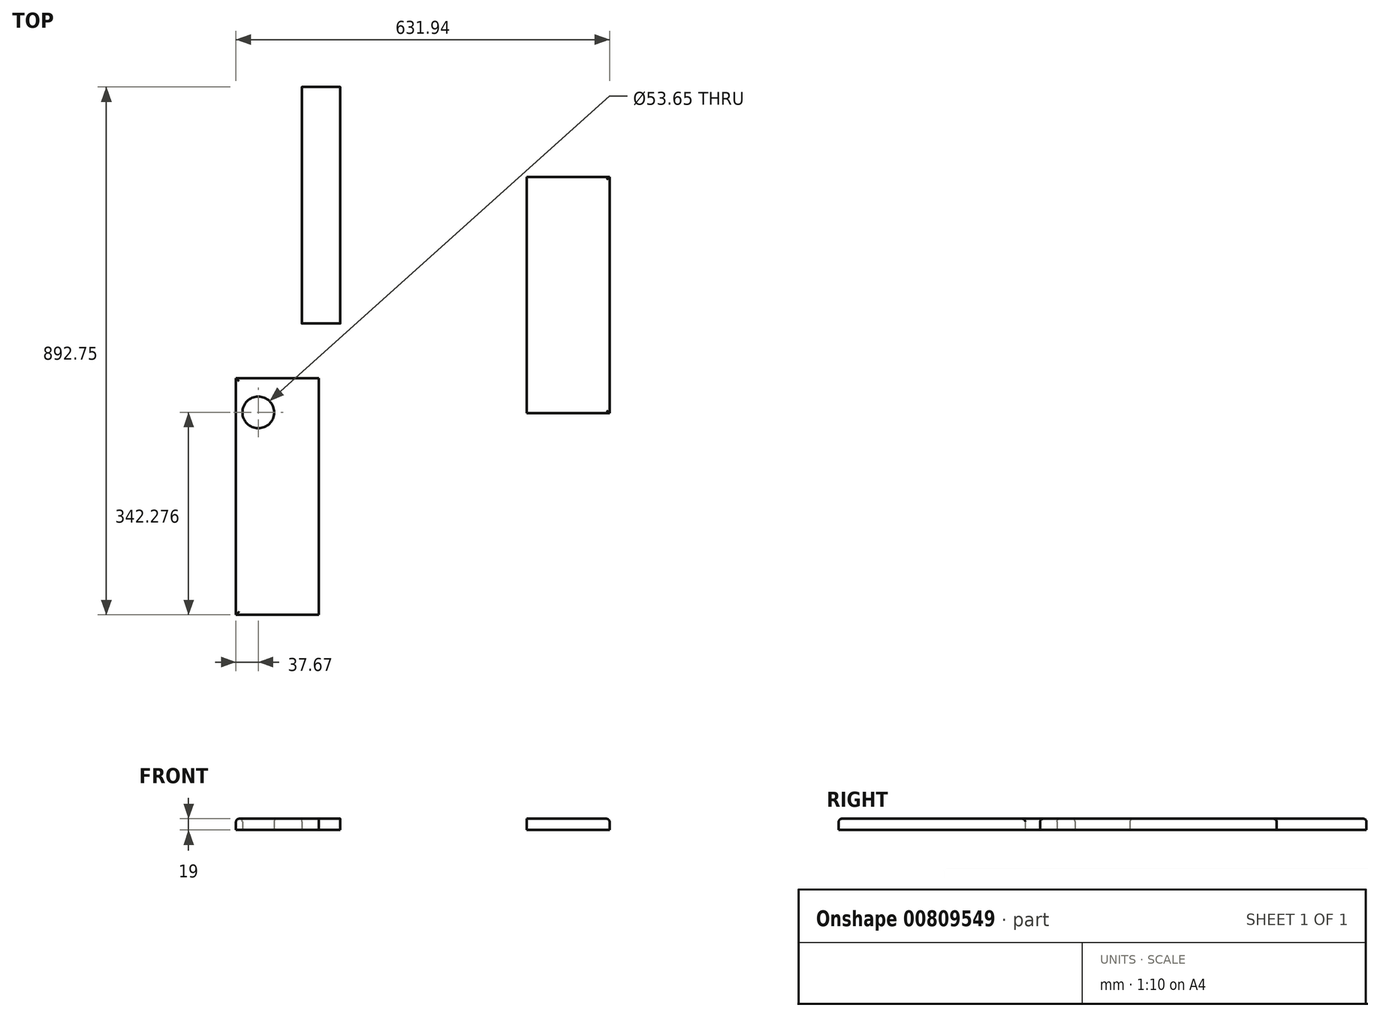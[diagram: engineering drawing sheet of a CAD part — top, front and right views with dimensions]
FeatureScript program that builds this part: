
annotation { "Feature Type Name" : "Feature", "Feature Type Description" : "" }
export const myFeature = defineFeature(function(context is Context, id is Id, definition is map)
    precondition{}
    {
        {
            var Q0;
            Q0=qCreatedBy(makeId("Top.planeOp"),FACE);
            var sketch = newSketch(context, id + "F0", { "sketchPlane" : qUnion([Q0])});
            skLineSegment(sketch, "E0.bottom", {"start": v(-171.23, -176.51) * mm, "end": v(-31.23, -176.51) * mm});
            skLineSegment(sketch, "E0.top", {"start": v(-171.23, 223.49) * mm, "end": v(-31.23, 223.49) * mm});
            skLineSegment(sketch, "E0.left", {"start": v(-171.23, -176.51) * mm, "end": v(-171.23, 223.49) * mm});
            skLineSegment(sketch, "E0.right", {"start": v(-31.23, -176.51) * mm, "end": v(-31.23, 223.49) * mm});
            skSolve(sketch);
        }
        {
            var Q0;
            Q0=makeQuery(id+"F0.imprint","IMPRINT",FACE,{"disambiguationData":[TD([[makeQuery(id+"F0.imprint","IMPRINT",EDGE,{"derivedFrom":sQuery(id+"F0.wireOp",EDGE,"E0.bottom")}),1.0]])]});
            extrude(context, id + "F1", {"entities" : qUnion([Q0]), "depth" : 19 * mm, "offsetDistance" : 25 * mm});
        }
        {
            var Q0;
            Q0=qCreatedBy(makeId("Top.planeOp"),FACE);
            var sketch = newSketch(context, id + "F2", { "sketchPlane" : qUnion([Q0])});
            skLineSegment(sketch, "E1.bottom", {"start": v(-551.77, 375.45) * mm, "end": v(-486.77, 375.45) * mm});
            skLineSegment(sketch, "E1.top", {"start": v(-551.77, -24.55) * mm, "end": v(-486.77, -24.55) * mm});
            skLineSegment(sketch, "E1.left", {"start": v(-551.77, 375.45) * mm, "end": v(-551.77, -24.55) * mm});
            skLineSegment(sketch, "E1.right", {"start": v(-486.77, 375.45) * mm, "end": v(-486.77, -24.55) * mm});
            skSolve(sketch);
        }
        {
            var Q0;
            Q0=makeQuery(id+"F2.imprint","IMPRINT",FACE,{"disambiguationData":[TD([[makeQuery(id+"F2.imprint","IMPRINT",EDGE,{"derivedFrom":sQuery(id+"F2.wireOp",EDGE,"E1.bottom")}),-1.0]])]});
            extrude(context, id + "F3", {"entities" : qUnion([Q0]), "depth" : 19 * mm, "offsetDistance" : 25 * mm});
        }
        {
            var Q0;
            Q0=qCreatedBy(makeId("Top.planeOp"),FACE);
            var sketch = newSketch(context, id + "F4", { "sketchPlane" : qUnion([Q0])});
            skLineSegment(sketch, "E2.bottom", {"start": v(-663.17, -117.3) * mm, "end": v(-523.17, -117.3) * mm});
            skLineSegment(sketch, "E2.top", {"start": v(-663.17, -517.3) * mm, "end": v(-523.17, -517.3) * mm});
            skLineSegment(sketch, "E2.left", {"start": v(-663.17, -117.3) * mm, "end": v(-663.17, -517.3) * mm});
            skLineSegment(sketch, "E2.right", {"start": v(-523.17, -117.3) * mm, "end": v(-523.17, -517.3) * mm});
            skCircle(sketch, "E3", {"center": v(-625.5, -175.02) * mm, "radius": 26.82 * mm});
            skSolve(sketch);
        }
        {
            var Q0;
            Q0 = qSketchRegion(id + "F4", true);
            extrude(context, id + "F5", {"entities" : qUnion([Q0]), "depth" : 19 * mm, "offsetDistance" : 25 * mm});
        }
        {
            var Q0;
            Q0=makeQuery(id+"F5.opExtrude","CAP_EDGE",EDGE,{"disambiguationData":[OSD([sQuery(id+"F4.wireOp",EDGE,"E2.left")])],"isStart":false});
            var Q1;
            Q1=makeQuery(id+"F5.opExtrude","CAP_EDGE",EDGE,{"disambiguationData":[OSD([sQuery(id+"F4.wireOp",EDGE,"E2.top")])],"isStart":false});
            var Q2;
            Q2=makeQuery(id+"F5.opExtrude","CAP_EDGE",EDGE,{"disambiguationData":[OSD([sQuery(id+"F4.wireOp",EDGE,"E2.bottom")])],"isStart":false});
            var Q3;
            Q3=makeQuery(id+"F3.opExtrude","CAP_EDGE",EDGE,{"disambiguationData":[OSD([sQuery(id+"F2.wireOp",EDGE,"E1.top")])],"isStart":false});
            var Q4;
            Q4=makeQuery(id+"F3.opExtrude","CAP_EDGE",EDGE,{"disambiguationData":[OSD([sQuery(id+"F2.wireOp",EDGE,"E1.bottom")])],"isStart":false});
            var Q5;
            Q5=makeQuery(id+"F1.opExtrude","CAP_EDGE",EDGE,{"disambiguationData":[OSD([sQuery(id+"F0.wireOp",EDGE,"E0.bottom")])],"isStart":false});
            var Q6;
            Q6=makeQuery(id+"F1.opExtrude","CAP_EDGE",EDGE,{"disambiguationData":[OSD([sQuery(id+"F0.wireOp",EDGE,"E0.right")])],"isStart":false});
            var Q7;
            Q7=makeQuery(id+"F1.opExtrude","CAP_EDGE",EDGE,{"disambiguationData":[OSD([sQuery(id+"F0.wireOp",EDGE,"E0.top")])],"isStart":false});
            fillet(context, id + "F6", {"entities" : qUnion([Q0, Q1, Q2, Q3, Q4, Q5, Q6, Q7]), "radius" : 5 * mm, "tangentPropagation" : true, "allowEdgeOverflow" : false});
        }
        {
            var Q0;
            Q0=makeQuery(id+"F5.opExtrude","CAP_EDGE",EDGE,{"disambiguationData":[OSD([sQuery(id+"F4.wireOp",EDGE,"E3")])],"isStart":false});
            fillet(context, id + "F7", {"entities" : qUnion([Q0]), "radius" : 5 * mm, "tangentPropagation" : true, "allowEdgeOverflow" : false});
        }
    });
